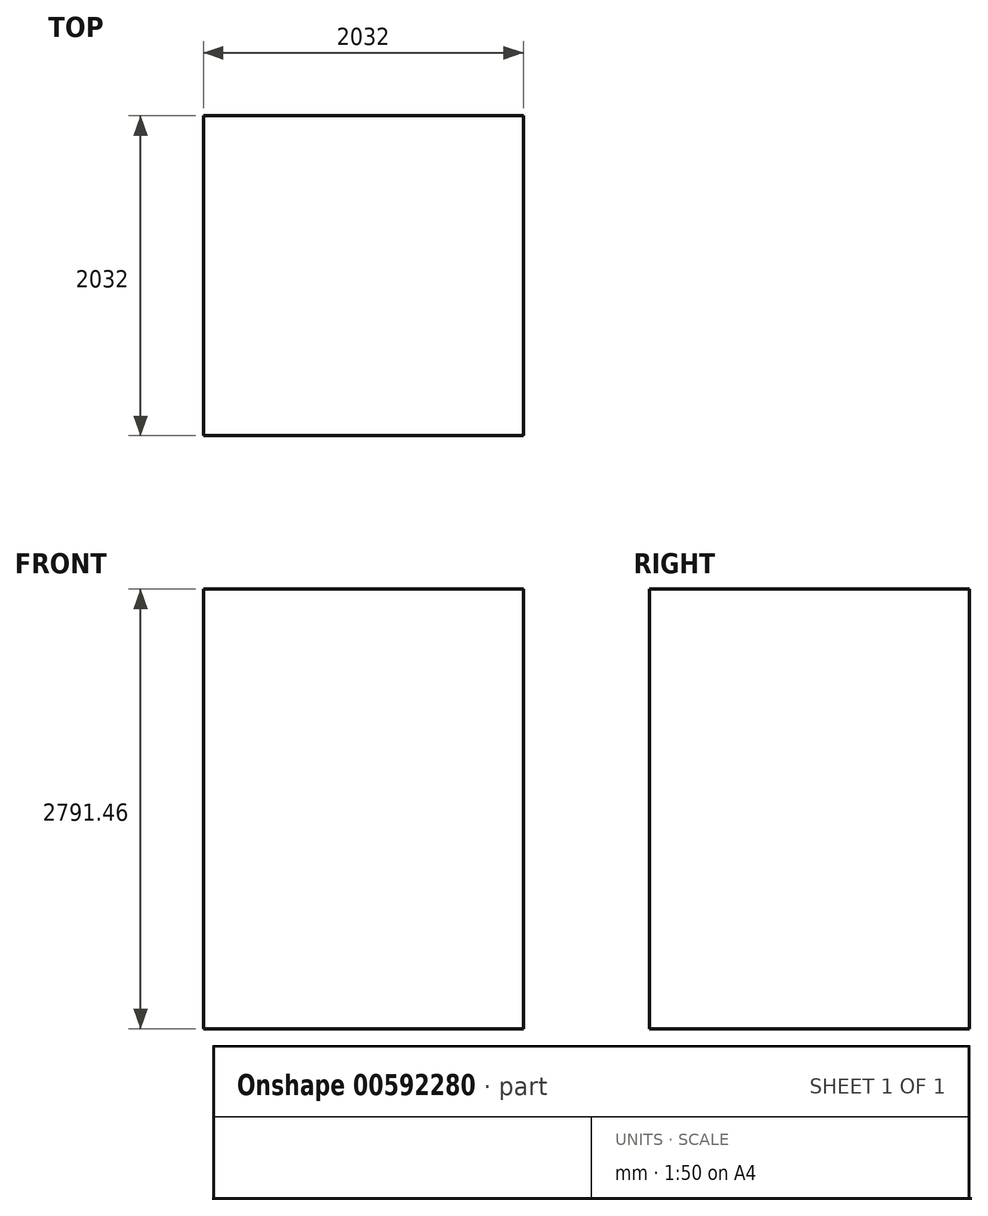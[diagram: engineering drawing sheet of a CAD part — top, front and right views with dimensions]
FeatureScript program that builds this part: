
annotation { "Feature Type Name" : "Feature", "Feature Type Description" : "" }
export const myFeature = defineFeature(function(context is Context, id is Id, definition is map)
    precondition{}
    {
        {
            var Q0;
            Q0=qCreatedBy(makeId("Top.planeOp"),FACE);
            var sketch = newSketch(context, id + "F0", { "sketchPlane" : qUnion([Q0])});
            skLineSegment(sketch, "E0.bottom", {"start": v(1016, 1016) * mm, "end": v(-1016, 1016) * mm});
            skLineSegment(sketch, "E0.top", {"start": v(1016, -1016) * mm, "end": v(-1016, -1016) * mm});
            skLineSegment(sketch, "E0.left", {"start": v(1016, 1016) * mm, "end": v(1016, -1016) * mm});
            skLineSegment(sketch, "E0.right", {"start": v(-1016, 1016) * mm, "end": v(-1016, -1016) * mm});
            skPoint(sketch, "E0.middle", {"position": v(0, 0) * mm});
            skSolve(sketch);
        }
        {
            var Q0;
            Q0 = qSketchRegion(id + "F0", true);
            extrude(context, id + "F1", {"entities" : qUnion([Q0]), "depth" : 2791.46 * mm, "offsetDistance" : 25.4 * mm});
        }
    });
